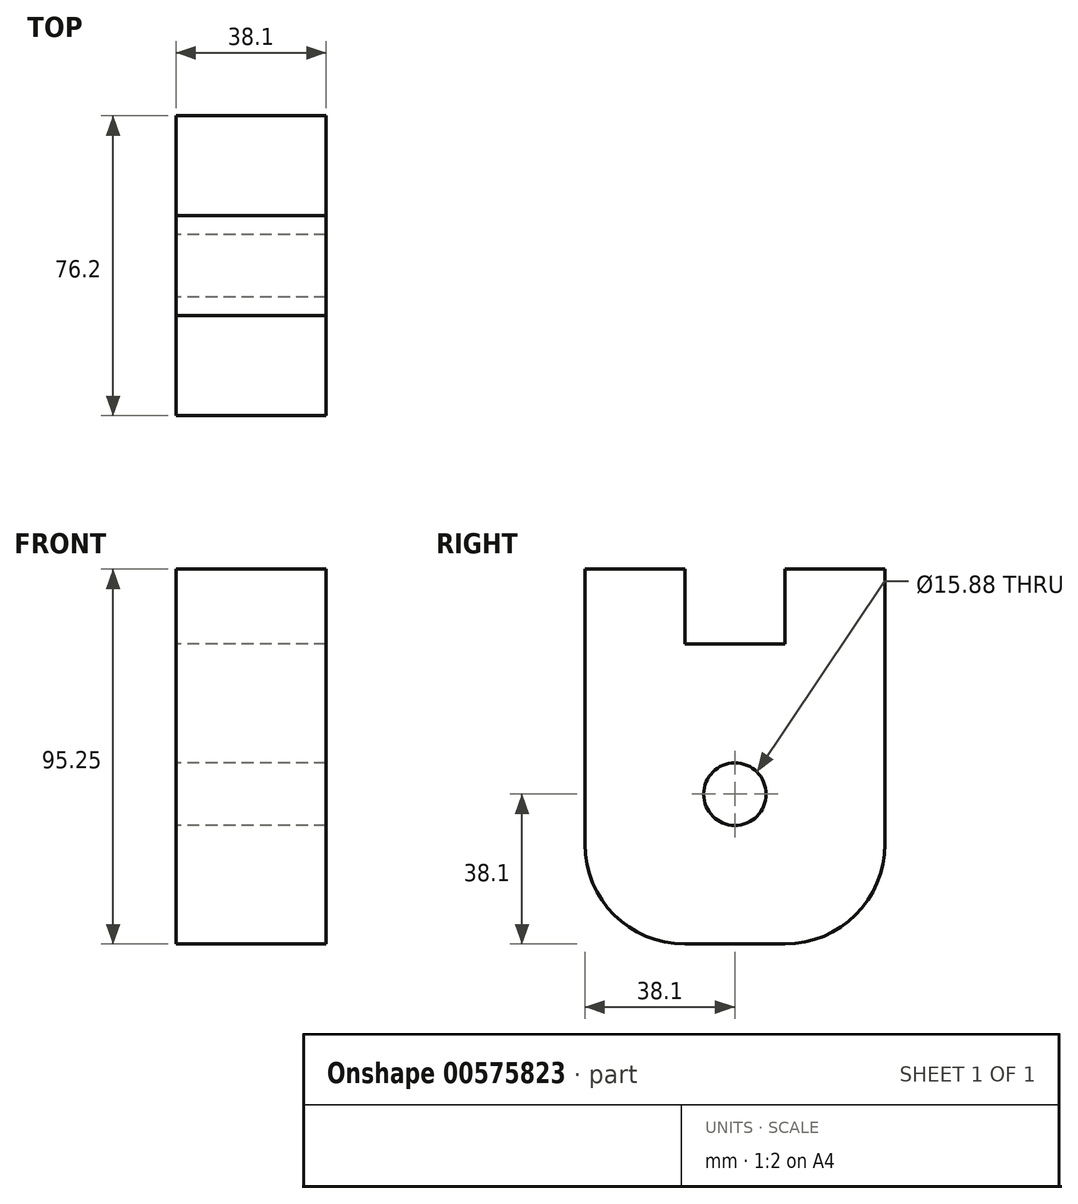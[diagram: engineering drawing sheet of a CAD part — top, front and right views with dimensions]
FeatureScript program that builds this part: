
annotation { "Feature Type Name" : "Feature", "Feature Type Description" : "" }
export const myFeature = defineFeature(function(context is Context, id is Id, definition is map)
    precondition{}
    {
        {
            var Q0;
            Q0=qCreatedBy(makeId("Top.planeOp"),FACE);
            var sketch = newSketch(context, id + "F0", { "sketchPlane" : qUnion([Q0])});
            skLineSegment(sketch, "E0.bottom", {"start": v(0, 0) * mm, "end": v(38.1, 0) * mm});
            skLineSegment(sketch, "E0.top", {"start": v(0, -76.2) * mm, "end": v(38.1, -76.2) * mm});
            skLineSegment(sketch, "E0.left", {"start": v(0, 0) * mm, "end": v(0, -76.2) * mm});
            skLineSegment(sketch, "E0.right", {"start": v(38.1, 0) * mm, "end": v(38.1, -76.2) * mm});
            skSolve(sketch);
        }
        {
            var Q0;
            Q0=makeQuery(id+"F0.imprint","IMPRINT",FACE,{"disambiguationData":[TD([[makeQuery(id+"F0.imprint","IMPRINT",EDGE,{"derivedFrom":sQuery(id+"F0.wireOp",EDGE,"E0.bottom")}),-1.0]])]});
            extrude(context, id + "F1", {"entities" : qUnion([Q0]), "depth" : 76.2 * mm, "offsetDistance" : 25.4 * mm});
        }
        {
            var Q0;
            Q0=makeQuery(id+"F1.opExtrude","SWEPT_FACE",FACE,{"disambiguationData":[OSD([sQuery(id+"F0.wireOp",EDGE,"E0.left")])]});
            var sketch = newSketch(context, id + "F2", { "sketchPlane" : qUnion([Q0])});
            skCircle(sketch, "E1", {"center": v(38.1, 38.1) * mm, "radius": 7.94 * mm});
            skSolve(sketch);
        }
        {
            var Q0;
            Q0=makeQuery(id+"F2.imprint","IMPRINT",FACE,{"disambiguationData":[TD([[makeQuery(id+"F2.imprint","IMPRINT",EDGE,{"derivedFrom":sQuery(id+"F2.wireOp",EDGE,"E1")}),1.0]])]});
            extrude(context, id + "F3", {"entities" : qUnion([Q0]), "operationType" : NewBodyOperationType.REMOVE, "oppositeDirection" : true, "depth" : 59.94 * mm, "offsetDistance" : 25.4 * mm});
        }
        {
            var Q0;
            Q0=makeQuery(id+"F1.opExtrude","CAP_FACE",FACE,{"disambiguationData":[OSD([sQuery(id+"F0.wireOp",EDGE,"E0.bottom"),sQuery(id+"F0.wireOp",EDGE,"E0.top"),sQuery(id+"F0.wireOp",EDGE,"E0.left"),sQuery(id+"F0.wireOp",EDGE,"E0.right")])],"isStart":false});
            var sketch = newSketch(context, id + "F4", { "sketchPlane" : qUnion([Q0])});
            skLineSegment(sketch, "E2.bottom", {"start": v(0, 0) * mm, "end": v(38.1, 0) * mm});
            skLineSegment(sketch, "E2.top", {"start": v(0, -25.4) * mm, "end": v(38.1, -25.4) * mm});
            skLineSegment(sketch, "E2.left", {"start": v(0, 0) * mm, "end": v(0, -25.4) * mm});
            skLineSegment(sketch, "E2.right", {"start": v(38.1, 0) * mm, "end": v(38.1, -25.4) * mm});
            skLineSegment(sketch, "E3.bottom", {"start": v(38.1, -76.2) * mm, "end": v(0, -76.2) * mm});
            skLineSegment(sketch, "E3.top", {"start": v(38.1, -50.8) * mm, "end": v(0, -50.8) * mm});
            skLineSegment(sketch, "E3.left", {"start": v(38.1, -76.2) * mm, "end": v(38.1, -50.8) * mm});
            skLineSegment(sketch, "E3.right", {"start": v(0, -76.2) * mm, "end": v(0, -50.8) * mm});
            skSolve(sketch);
        }
        {
            var Q0;
            Q0=makeQuery(id+"F4.imprint","IMPRINT",FACE,{"disambiguationData":[TD([[makeQuery(id+"F4.imprint","IMPRINT",EDGE,{"derivedFrom":sQuery(id+"F4.wireOp",EDGE,"E2.bottom")}),-1.0]])]});
            var Q1;
            Q1=makeQuery(id+"F4.imprint","IMPRINT",FACE,{"disambiguationData":[TD([[makeQuery(id+"F4.imprint","IMPRINT",EDGE,{"derivedFrom":sQuery(id+"F4.wireOp",EDGE,"E3.bottom")}),1.0]])]});
            extrude(context, id + "F5", {"entities" : qUnion([Q0, Q1]), "operationType" : NewBodyOperationType.ADD, "depth" : 19.05 * mm, "offsetDistance" : 25.4 * mm});
        }
        {
            var Q0;
            Q0=makeQuery(id+"F1.opExtrude","CAP_EDGE",EDGE,{"disambiguationData":[OSD([sQuery(id+"F0.wireOp",EDGE,"E0.bottom")])],"isStart":true});
            var Q1;
            Q1=makeQuery(id+"F1.opExtrude","CAP_EDGE",EDGE,{"disambiguationData":[OSD([sQuery(id+"F0.wireOp",EDGE,"E0.top")])],"isStart":true});
            fillet(context, id + "F6", {"entities" : qUnion([Q0, Q1]), "radius" : 25.4 * mm, "tangentPropagation" : true, "allowEdgeOverflow" : false});
        }
    });
